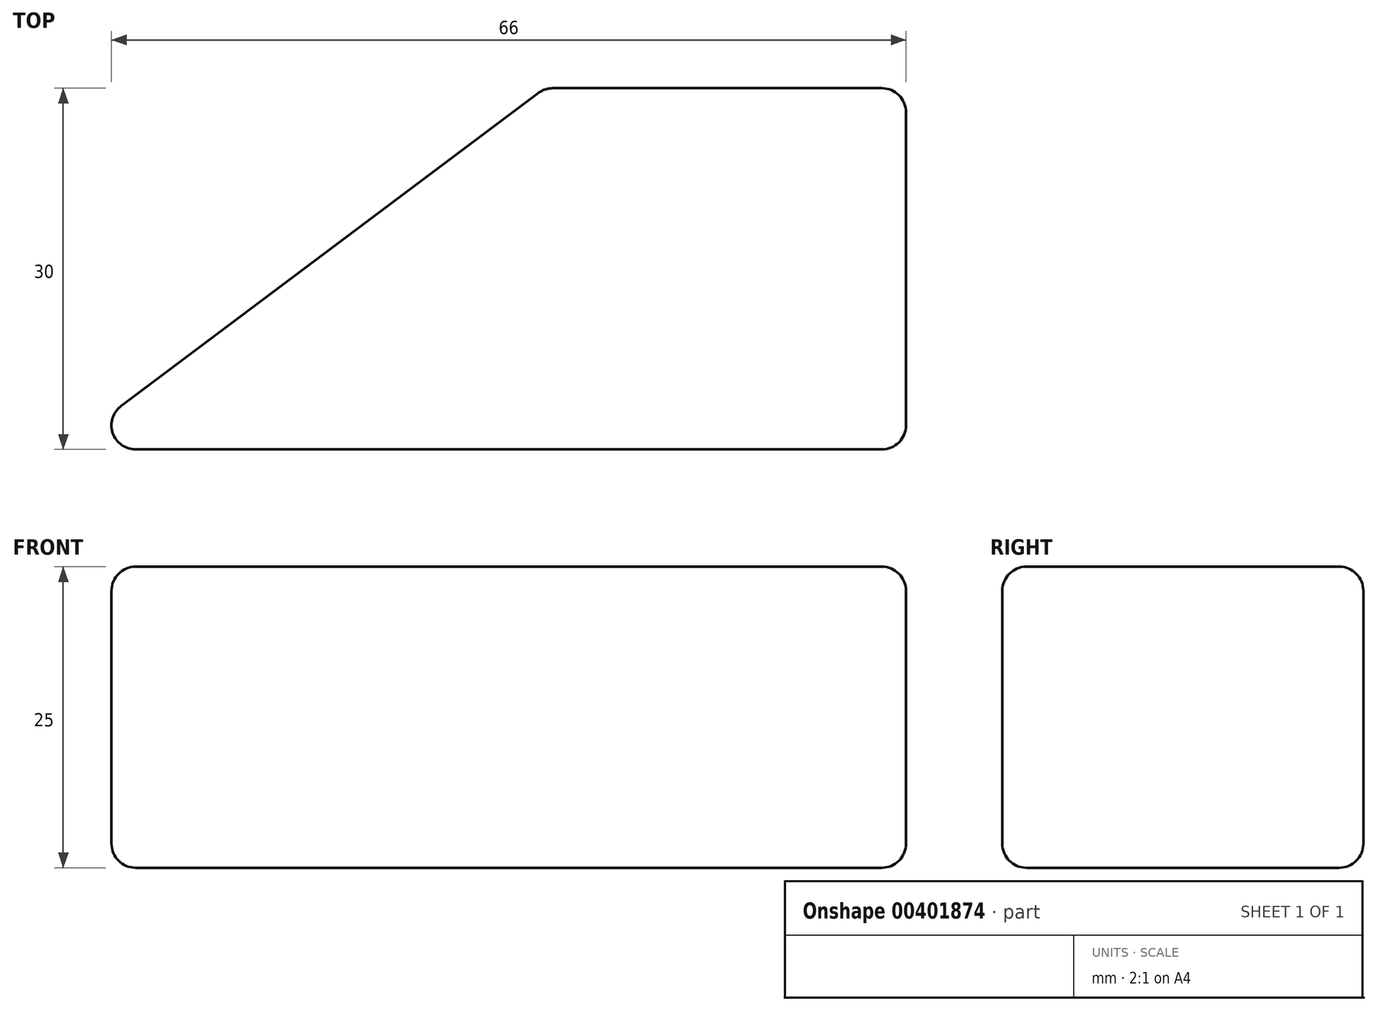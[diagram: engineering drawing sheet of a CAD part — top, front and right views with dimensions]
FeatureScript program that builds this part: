
annotation { "Feature Type Name" : "Feature", "Feature Type Description" : "" }
export const myFeature = defineFeature(function(context is Context, id is Id, definition is map)
    precondition{}
    {
        {
            var Q0;
            Q0=qCreatedBy(makeId("Top.planeOp"),FACE);
            var sketch = newSketch(context, id + "F0", { "sketchPlane" : qUnion([Q0])});
            skLineSegment(sketch, "E0.bottom", {"start": v(-23.43, 37.1) * mm, "end": v(6.57, 37.1) * mm});
            skLineSegment(sketch, "E0.top", {"start": v(-23.43, 7.1) * mm, "end": v(6.57, 7.1) * mm});
            skLineSegment(sketch, "E0.right", {"start": v(6.57, 37.1) * mm, "end": v(6.57, 7.1) * mm});
            skLineSegment(sketch, "E1", {"start": v(-23.43, 37.1) * mm, "end": v(-63.43, 7.1) * mm});
            skLineSegment(sketch, "E2", {"start": v(-63.43, 7.1) * mm, "end": v(-23.43, 7.1) * mm});
            skSolve(sketch);
        }
        {
            var Q0;
            Q0=makeQuery(id+"F0.imprint","IMPRINT",FACE,{"disambiguationData":[TD([[makeQuery(id+"F0.imprint","IMPRINT",EDGE,{"derivedFrom":sQuery(id+"F0.wireOp",EDGE,"E0.bottom")}),-1.0]])]});
            extrude(context, id + "F1", {"entities" : qUnion([Q0]), "depth" : 25 * mm});
        }
        {
            var Q0;
            Q0=makeQuery(id+"F1.opExtrude","CAP_FACE",FACE,{"disambiguationData":[OSD([sQuery(id+"F0.wireOp",EDGE,"E0.bottom"),sQuery(id+"F0.wireOp",EDGE,"E0.top"),sQuery(id+"F0.wireOp",EDGE,"E0.right"),sQuery(id+"F0.wireOp",EDGE,"E1"),sQuery(id+"F0.wireOp",EDGE,"E2")])],"isStart":false});
            var Q1;
            Q1=makeQuery(id+"F1.opExtrude","SWEPT_FACE",FACE,{"disambiguationData":[OSD([sQuery(id+"F0.wireOp",EDGE,"E0.top"),sQuery(id+"F0.wireOp",EDGE,"E2")])]});
            var Q2;
            Q2=makeQuery(id+"F1.opExtrude","SWEPT_FACE",FACE,{"disambiguationData":[OSD([sQuery(id+"F0.wireOp",EDGE,"E1")])]});
            var Q3;
            Q3=makeQuery(id+"F1.opExtrude","SWEPT_EDGE",EDGE,{"disambiguationData":[OSD([sQuery(id+"F0.wireOp",EDGE,"E0.bottom"),sQuery(id+"F0.wireOp",EDGE,"E0.right")])]});
            var Q4;
            Q4=makeQuery(id+"F1.opExtrude","CAP_EDGE",EDGE,{"disambiguationData":[OSD([sQuery(id+"F0.wireOp",EDGE,"E0.bottom")])],"isStart":true});
            var Q5;
            Q5=makeQuery(id+"F1.opExtrude","CAP_EDGE",EDGE,{"disambiguationData":[OSD([sQuery(id+"F0.wireOp",EDGE,"E0.right")])],"isStart":true});
            fillet(context, id + "F2", {"entities" : qUnion([Q0, Q1, Q2, Q3, Q4, Q5]), "radius" : 2 * mm, "tangentPropagation" : true, "allowEdgeOverflow" : false});
        }
    });
